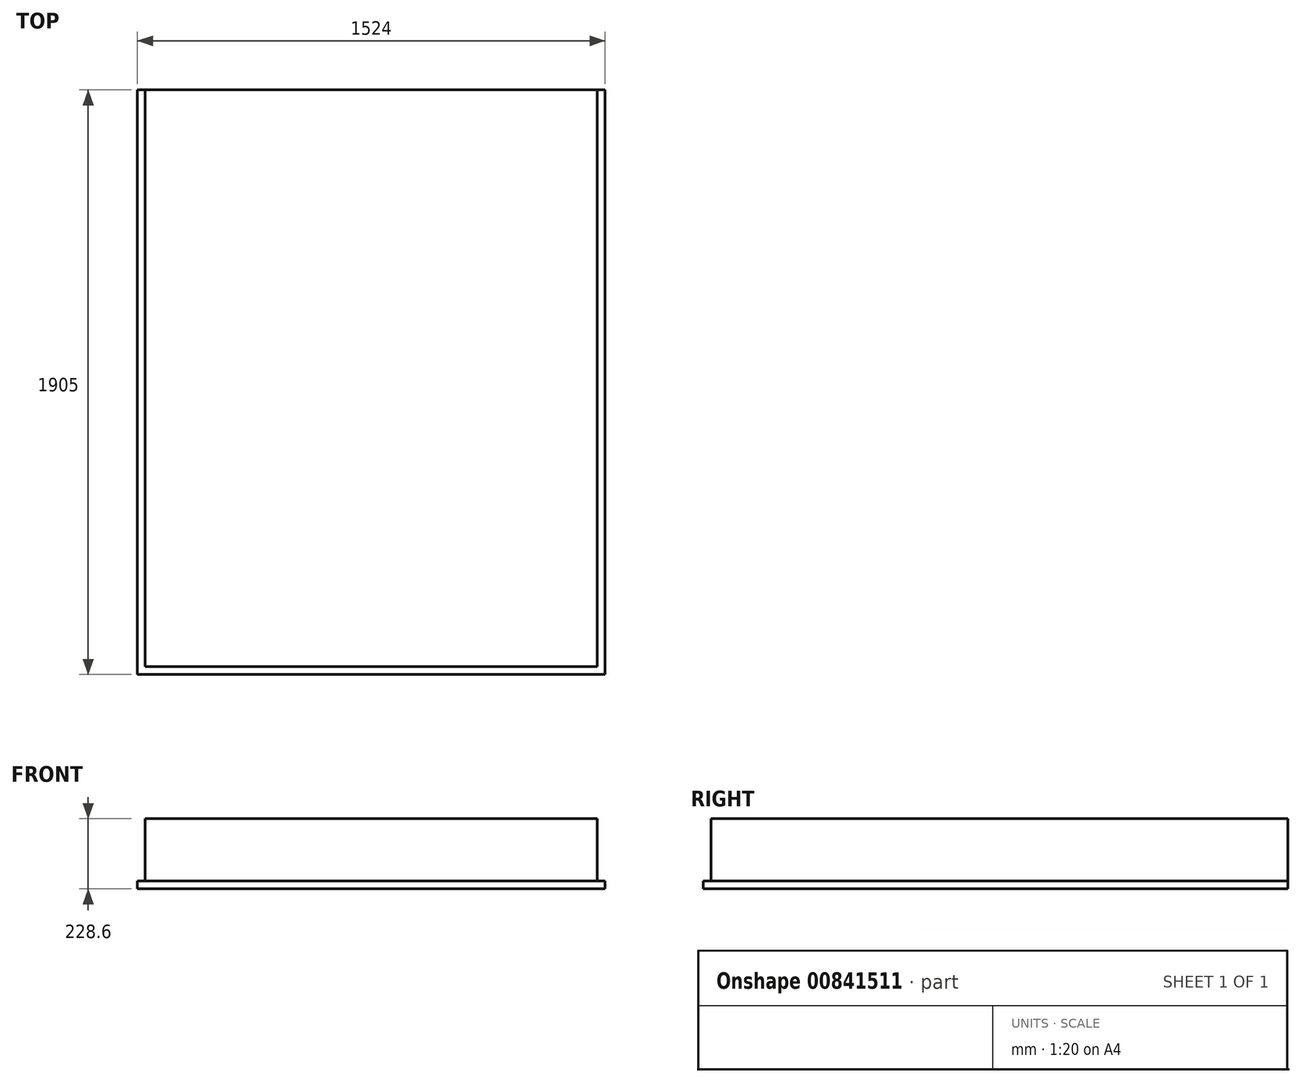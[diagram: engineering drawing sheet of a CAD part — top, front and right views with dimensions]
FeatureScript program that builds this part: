
annotation { "Feature Type Name" : "Feature", "Feature Type Description" : "" }
export const myFeature = defineFeature(function(context is Context, id is Id, definition is map)
    precondition{}
    {
        {
            var Q0;
            Q0=qCreatedBy(makeId("Top.planeOp"),FACE);
            var sketch = newSketch(context, id + "F0", { "sketchPlane" : qUnion([Q0])});
            skLineSegment(sketch, "E0.bottom", {"start": v(0, 0) * mm, "end": v(1524, 0) * mm});
            skLineSegment(sketch, "E0.top", {"start": v(0, 1905) * mm, "end": v(1524, 1905) * mm});
            skLineSegment(sketch, "E0.left", {"start": v(0, 0) * mm, "end": v(0, 1905) * mm});
            skLineSegment(sketch, "E0.right", {"start": v(1524, 0) * mm, "end": v(1524, 1905) * mm});
            skSolve(sketch);
        }
        {
            var Q0;
            Q0=makeQuery(id+"F0.imprint","IMPRINT",FACE,{"disambiguationData":[TD([[makeQuery(id+"F0.imprint","IMPRINT",EDGE,{"derivedFrom":sQuery(id+"F0.wireOp",EDGE,"E0.bottom")}),1.0]])]});
            extrude(context, id + "F1", {"entities" : qUnion([Q0]), "depth" : 25.4 * mm, "offsetDistance" : 25.4 * mm});
        }
        {
            var Q0;
            Q0=makeQuery(id+"F1.opExtrude","CAP_FACE",FACE,{"disambiguationData":[OSD([sQuery(id+"F0.wireOp",EDGE,"E0.bottom"),sQuery(id+"F0.wireOp",EDGE,"E0.top"),sQuery(id+"F0.wireOp",EDGE,"E0.left"),sQuery(id+"F0.wireOp",EDGE,"E0.right")])],"isStart":false});
            var sketch = newSketch(context, id + "F2", { "sketchPlane" : qUnion([Q0])});
            skLineSegment(sketch, "E1.bottom", {"start": v(25.4, 1905) * mm, "end": v(1498.6, 1905) * mm});
            skLineSegment(sketch, "E1.top", {"start": v(25.4, 25.4) * mm, "end": v(1498.6, 25.4) * mm});
            skLineSegment(sketch, "E1.left", {"start": v(25.4, 1905) * mm, "end": v(25.4, 25.4) * mm});
            skLineSegment(sketch, "E1.right", {"start": v(1498.6, 1905) * mm, "end": v(1498.6, 25.4) * mm});
            skSolve(sketch);
        }
        {
            var Q0;
            Q0=qSketchRegion(id+"F2",true);
            extrude(context, id + "F3", {"entities" : qUnion([Q0]), "operationType" : NewBodyOperationType.ADD, "depth" : 203.2 * mm, "offsetDistance" : 25.4 * mm});
        }
    });
